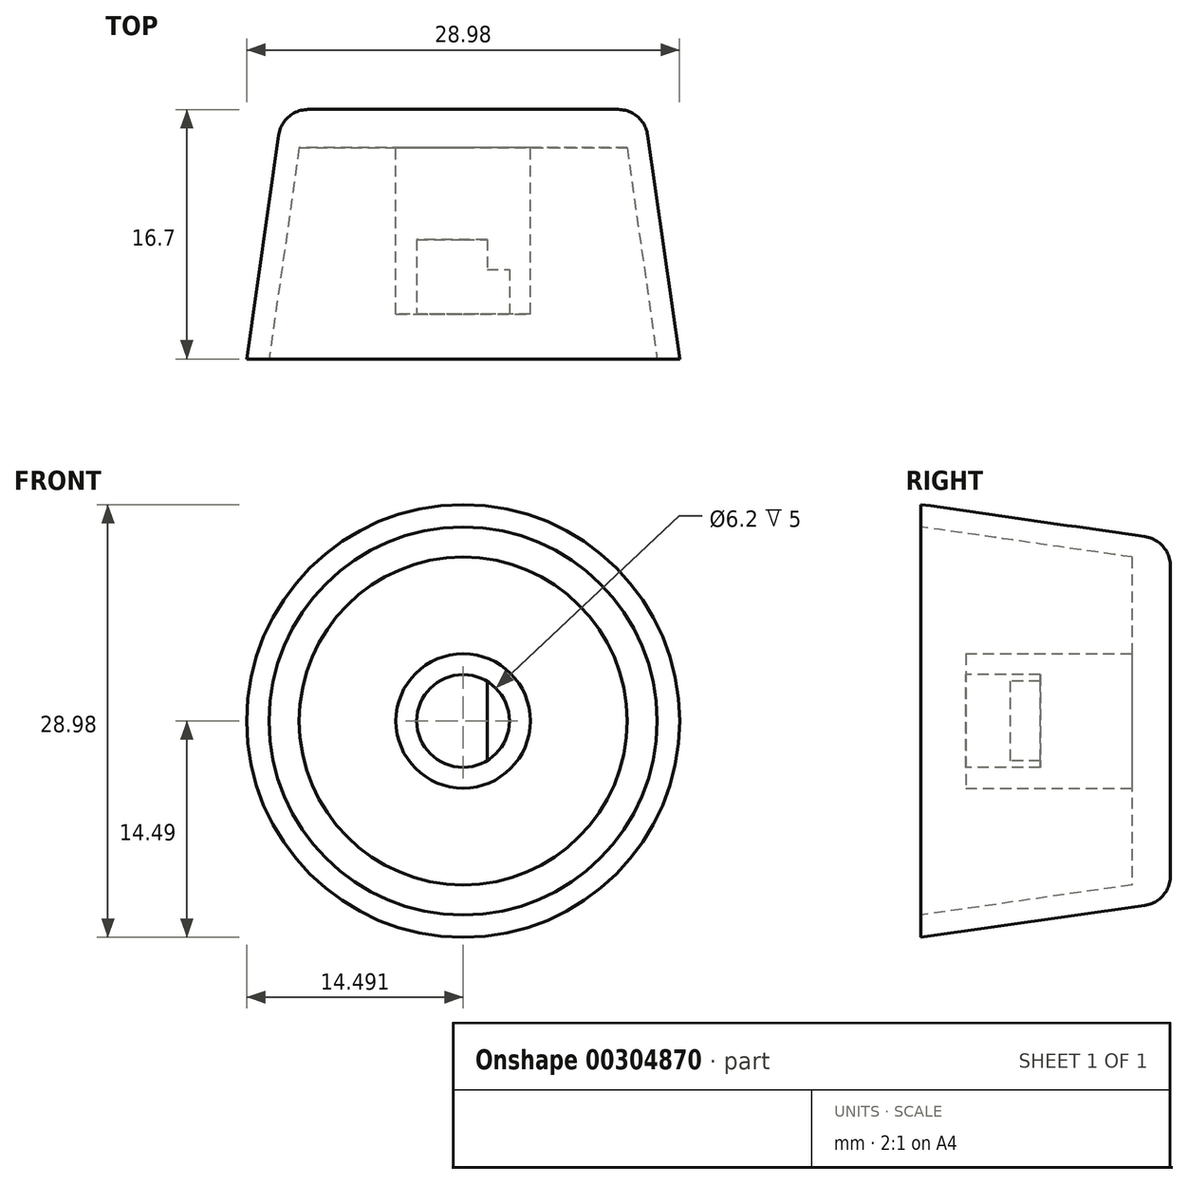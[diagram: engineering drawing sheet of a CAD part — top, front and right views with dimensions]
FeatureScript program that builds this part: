
annotation { "Feature Type Name" : "Feature", "Feature Type Description" : "" }
export const myFeature = defineFeature(function(context is Context, id is Id, definition is map)
    precondition{}
    {
        {
            var Q0;
            Q0=qCreatedBy(makeId("Top.planeOp"),FACE);
            var sketch = newSketch(context, id + "F0", { "sketchPlane" : qUnion([Q0])});
            skLineSegment(sketch, "E0", {"start": v(15.15, 0) * mm, "end": v(12.75, 16.7) * mm});
            skLineSegment(sketch, "E1", {"start": v(12.75, 16.7) * mm, "end": v(-11.47, 16.7) * mm});
            skLineSegment(sketch, "E2", {"start": v(-11.47, 16.7) * mm, "end": v(-13.85, 0) * mm});
            skLineSegment(sketch, "E3", {"start": v(-13.85, 0) * mm, "end": v(-12.35, 0) * mm});
            skLineSegment(sketch, "E4", {"start": v(-12.35, 0) * mm, "end": v(-10.33, 14.14) * mm});
            skLineSegment(sketch, "E5", {"start": v(-10.33, 14.14) * mm, "end": v(-3.86, 14.14) * mm});
            skLineSegment(sketch, "E6", {"start": v(-3.86, 14.14) * mm, "end": v(-3.86, 3) * mm});
            skLineSegment(sketch, "E7", {"start": v(-3.86, 3) * mm, "end": v(5.14, 3) * mm});
            skLineSegment(sketch, "E8", {"start": v(5.14, 3) * mm, "end": v(5.14, 14.14) * mm});
            skLineSegment(sketch, "E9", {"start": v(5.14, 14.14) * mm, "end": v(11.62, 14.14) * mm});
            skLineSegment(sketch, "E10", {"start": v(11.62, 14.14) * mm, "end": v(13.65, 0) * mm});
            skLineSegment(sketch, "E11", {"start": v(13.65, 0) * mm, "end": v(15.15, 0) * mm});
            skPoint(sketch, "E12", {"position": v(0.64, 16.7) * mm});
            skPoint(sketch, "E13", {"position": v(-11.47, 16.7) * mm});
            skPoint(sketch, "E14", {"position": v(12.75, 16.7) * mm});
            skLineSegment(sketch, "E15", {"start": v(0.64, 16.7) * mm, "end": v(0.64, -10.32) * mm});
            skSolve(sketch);
        }
        {
            var Q0;
            {var subQ0=sQuery(id+"F0.wireOp",EDGE,"E2");Q0=makeQuery(id+"F0.imprint","IMPRINT",FACE,{"disambiguationData":[TD([[makeQuery(id+"F0.imprint","IMPRINT",EDGE,{"derivedFrom":subQ0}),1.0]])]});}
            var Q1;
            Q1=sQuery(id+"F0.wireOp",EDGE,"E15");
            revolve(context, id + "F1", {"entities" : qUnion([Q0]), "axis" : qUnion([Q1]), "revolveType" : RevolveType.FULL});
        }
        {
            var Q0;
            Q0=makeQuery(id+"F1.opRevolve","SWEPT_EDGE",EDGE,{"disambiguationData":[OSD([sQuery(id+"F0.wireOp",EDGE,"E1"),sQuery(id+"F0.wireOp",EDGE,"E2")])]});
            fillet(context, id + "F2", {"entities" : qUnion([Q0]), "radius" : 2 * mm, "tangentPropagation" : true, "allowEdgeOverflow" : false});
        }
        {
            var Q0;
            Q0=makeQuery(id+"F1.opRevolve","SWEPT_FACE",FACE,{"disambiguationData":[OSD([sQuery(id+"F0.wireOp",EDGE,"E7")])]});
            var sketch = newSketch(context, id + "F3", { "sketchPlane" : qUnion([Q0])});
            skCircle(sketch, "E16", {"center": v(0.64, 0) * mm, "radius": 3.1 * mm});
            skLineSegment(sketch, "E17", {"start": v(2.24, -2.66) * mm, "end": v(2.24, 2.66) * mm});
            skSolve(sketch);
        }
        {
            var Q0;
            {var subQ0=sQuery(id+"F3.wireOp",EDGE,"E17");Q0=makeQuery(id+"F3.imprint","IMPRINT",FACE,{"disambiguationData":[TD([[makeQuery(id+"F3.imprint","IMPRINT",EDGE,{"derivedFrom":subQ0}),-1.0]])]});}
            var Q1;
            {var subQ0=sQuery(id+"F3.wireOp",EDGE,"E17");Q1=makeQuery(id+"F3.imprint","IMPRINT",FACE,{"disambiguationData":[TD([[makeQuery(id+"F3.imprint","IMPRINT",EDGE,{"derivedFrom":subQ0}),1.0]])]});}
            extrude(context, id + "F4", {"entities" : qUnion([Q0, Q1]), "operationType" : NewBodyOperationType.REMOVE, "oppositeDirection" : true, "depth" : 3 * mm});
        }
        {
            var Q0;
            {var subQ0=sQuery(id+"F3.wireOp",EDGE,"E17");Q0=makeQuery(id+"F3.imprint","IMPRINT",FACE,{"disambiguationData":[TD([[makeQuery(id+"F3.imprint","IMPRINT",EDGE,{"derivedFrom":subQ0}),1.0]])]});}
            extrude(context, id + "F5", {"entities" : qUnion([Q0]), "operationType" : NewBodyOperationType.REMOVE, "oppositeDirection" : true, "depth" : 5 * mm});
        }
    });
